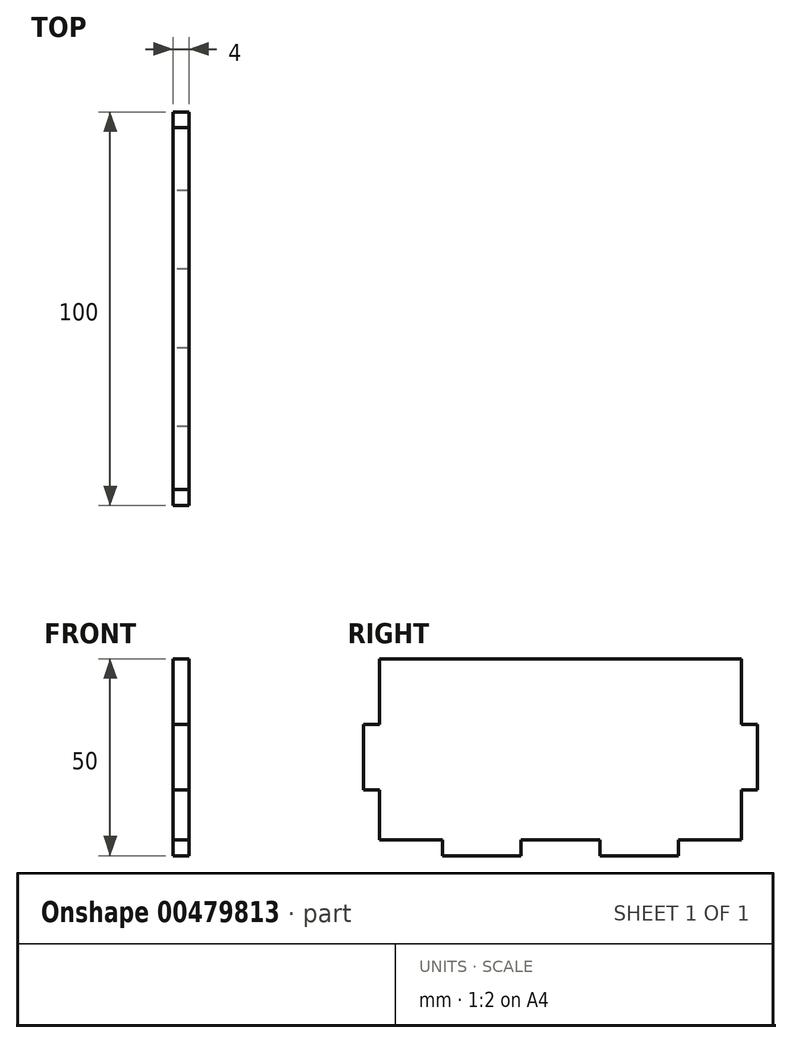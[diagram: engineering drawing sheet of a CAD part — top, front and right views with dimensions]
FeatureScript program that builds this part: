
annotation { "Feature Type Name" : "Feature", "Feature Type Description" : "" }
export const myFeature = defineFeature(function(context is Context, id is Id, definition is map)
    precondition{}
    {
        {
            var Q0;
            Q0=qCreatedBy(makeId("Right.planeOp"),FACE);
            var sketch = newSketch(context, id + "F0", { "sketchPlane" : qUnion([Q0])});
            skLineSegment(sketch, "E0.bottom", {"start": v(0, 0) * mm, "end": v(100, 0) * mm});
            skLineSegment(sketch, "E0.top", {"start": v(0, 50) * mm, "end": v(100, 50) * mm});
            skLineSegment(sketch, "E0.left", {"start": v(0, 0) * mm, "end": v(0, 50) * mm});
            skLineSegment(sketch, "E0.right", {"start": v(100, 0) * mm, "end": v(100, 50) * mm});
            skSolve(sketch);
        }
        {
            var Q0;
            Q0 = qSketchRegion(id + "F0", true);
            extrude(context, id + "F1", {"entities" : qUnion([Q0]), "depth" : 4 * mm});
        }
        {
            var Q0;
            Q0=qCreatedBy(makeId("Right.planeOp"),FACE);
            var sketch = newSketch(context, id + "F2", { "sketchPlane" : qUnion([Q0])});
            skLineSegment(sketch, "E1.bottom", {"start": v(0, 0) * mm, "end": v(4, 0) * mm});
            skLineSegment(sketch, "E1.top", {"start": v(0, 16.67) * mm, "end": v(4, 16.67) * mm});
            skLineSegment(sketch, "E1.left", {"start": v(0, 0) * mm, "end": v(0, 16.67) * mm});
            skLineSegment(sketch, "E1.right", {"start": v(4, 0) * mm, "end": v(4, 16.67) * mm});
            skLineSegment(sketch, "E2.bottom", {"start": v(0, 33.33) * mm, "end": v(4, 33.33) * mm});
            skLineSegment(sketch, "E2.top", {"start": v(0, 50) * mm, "end": v(4, 50) * mm});
            skLineSegment(sketch, "E2.left", {"start": v(0, 33.33) * mm, "end": v(0, 50) * mm});
            skLineSegment(sketch, "E2.right", {"start": v(4, 33.33) * mm, "end": v(4, 50) * mm});
            skLineSegment(sketch, "E3.bottom", {"start": v(0, 0) * mm, "end": v(20, 0) * mm});
            skLineSegment(sketch, "E3.top", {"start": v(0, 4) * mm, "end": v(20, 4) * mm});
            skLineSegment(sketch, "E3.left", {"start": v(0, 0) * mm, "end": v(0, 4) * mm});
            skLineSegment(sketch, "E3.right", {"start": v(20, 0) * mm, "end": v(20, 4) * mm});
            skLineSegment(sketch, "E4.bottom", {"start": v(40, 0) * mm, "end": v(60, 0) * mm});
            skLineSegment(sketch, "E4.top", {"start": v(40, 4) * mm, "end": v(60, 4) * mm});
            skLineSegment(sketch, "E4.left", {"start": v(40, 0) * mm, "end": v(40, 4) * mm});
            skLineSegment(sketch, "E4.right", {"start": v(60, 0) * mm, "end": v(60, 4) * mm});
            skLineSegment(sketch, "E5.bottom", {"start": v(100, 0) * mm, "end": v(96, 0) * mm});
            skLineSegment(sketch, "E5.top", {"start": v(100, 16.67) * mm, "end": v(96, 16.67) * mm});
            skLineSegment(sketch, "E5.left", {"start": v(100, 0) * mm, "end": v(100, 16.67) * mm});
            skLineSegment(sketch, "E5.right", {"start": v(96, 0) * mm, "end": v(96, 16.67) * mm});
            skLineSegment(sketch, "E6.bottom", {"start": v(96, 50) * mm, "end": v(100, 50) * mm});
            skLineSegment(sketch, "E6.top", {"start": v(96, 33.33) * mm, "end": v(100, 33.33) * mm});
            skLineSegment(sketch, "E6.left", {"start": v(96, 50) * mm, "end": v(96, 33.33) * mm});
            skLineSegment(sketch, "E6.right", {"start": v(100, 50) * mm, "end": v(100, 33.33) * mm});
            skLineSegment(sketch, "E7.bottom", {"start": v(100, 0) * mm, "end": v(80, 0) * mm});
            skLineSegment(sketch, "E7.top", {"start": v(100, 4) * mm, "end": v(80, 4) * mm});
            skLineSegment(sketch, "E7.left", {"start": v(100, 0) * mm, "end": v(100, 4) * mm});
            skLineSegment(sketch, "E7.right", {"start": v(80, 0) * mm, "end": v(80, 4) * mm});
            skSolve(sketch);
        }
        {
            var Q0;
            Q0 = qSketchRegion(id + "F2", true);
            extrude(context, id + "F3", {"entities" : qUnion([Q0]), "operationType" : NewBodyOperationType.REMOVE, "depth" : 4 * mm});
        }
    });
